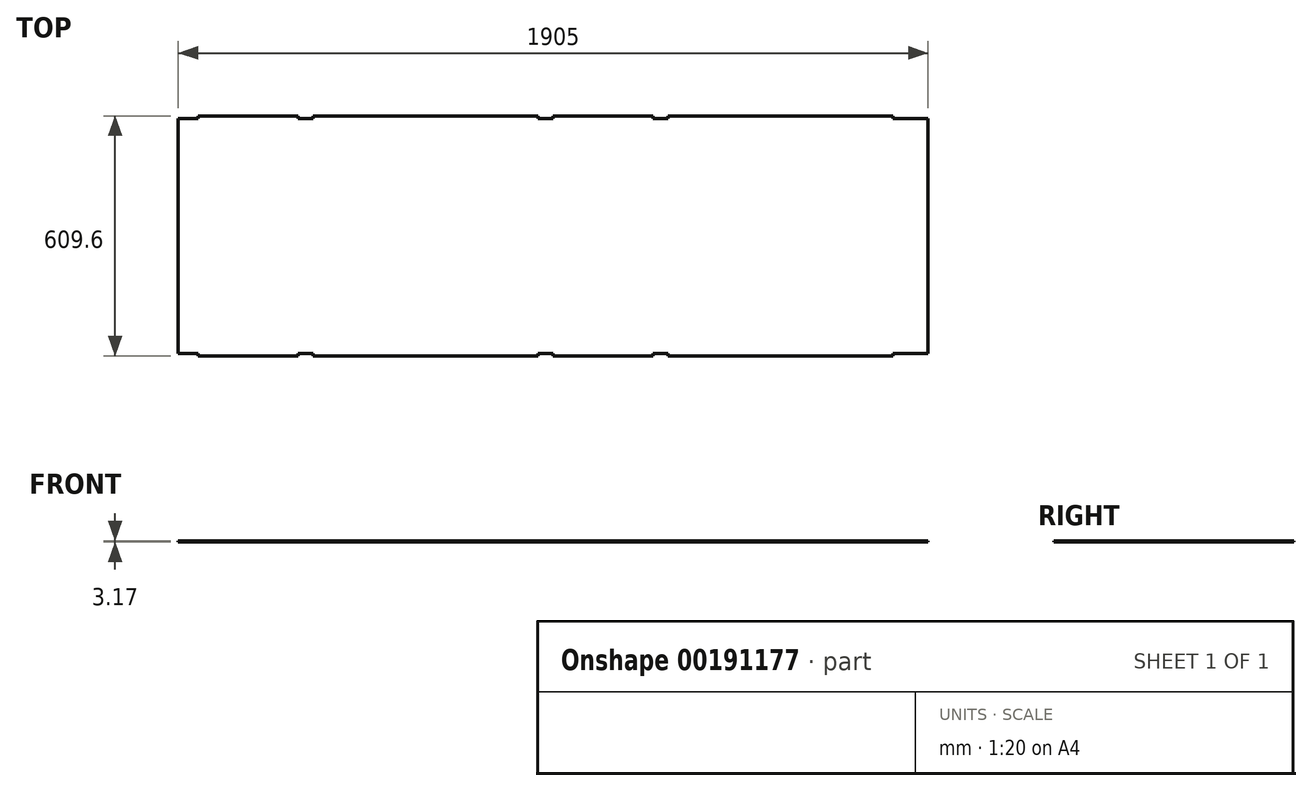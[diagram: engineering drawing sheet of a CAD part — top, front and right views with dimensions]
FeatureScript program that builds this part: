
annotation { "Feature Type Name" : "Feature", "Feature Type Description" : "" }
export const myFeature = defineFeature(function(context is Context, id is Id, definition is map)
    precondition{}
    {
        {
            var Q0;
            Q0=qCreatedBy(makeId("Top.planeOp"),FACE);
            var sketch = newSketch(context, id + "F0", { "sketchPlane" : qUnion([Q0])});
            skLineSegment(sketch, "E0.bottom", {"start": v(1276.35, -298.45) * mm, "end": v(-577.85, -298.45) * mm});
            skLineSegment(sketch, "E0.top", {"start": v(1276.35, 298.45) * mm, "end": v(-577.85, 298.45) * mm});
            skLineSegment(sketch, "E0.left", {"start": v(1276.35, -298.45) * mm, "end": v(1276.35, 298.45) * mm});
            skLineSegment(sketch, "E0.right", {"start": v(-577.85, -298.45) * mm, "end": v(-577.85, 298.45) * mm});
            skPoint(sketch, "E0.middle", {"position": v(349.25, 0) * mm});
            skLineSegment(sketch, "E1", {"start": v(615.95, 298.45) * mm, "end": v(615.95, -298.45) * mm, "construction": true});
            skLineSegment(sketch, "E2", {"start": v(577.85, 298.45) * mm, "end": v(577.85, -298.45) * mm, "construction": true});
            skLineSegment(sketch, "E3", {"start": v(-323.85, 298.45) * mm, "end": v(-323.85, -298.45) * mm, "construction": true});
            skLineSegment(sketch, "E4", {"start": v(-285.75, 298.45) * mm, "end": v(-285.75, -298.45) * mm, "construction": true});
            skLineSegment(sketch, "E5", {"start": v(285.75, 298.45) * mm, "end": v(285.75, -298.45) * mm, "construction": true});
            skLineSegment(sketch, "E6", {"start": v(323.85, 298.45) * mm, "end": v(323.85, -298.45) * mm, "construction": true});
            skLineSegment(sketch, "E7", {"start": v(1187.45, 298.45) * mm, "end": v(1187.45, -298.45) * mm, "construction": true});
            skSolve(sketch);
        }
        {
            var Q0;
            Q0 = qSketchRegion(id + "F0", true);
            extrude(context, id + "F1", {"entities" : qUnion([Q0]), "depth" : 3.17 * mm});
        }
        {
            var Q0;
            Q0=makeQuery(id+"F1.opExtrude","CAP_FACE",FACE,{"disambiguationData":[OSD([sQuery(id+"F0.wireOp",EDGE,"E0.bottom"),sQuery(id+"F0.wireOp",EDGE,"E0.top"),sQuery(id+"F0.wireOp",EDGE,"E0.left"),sQuery(id+"F0.wireOp",EDGE,"E0.right")])],"isStart":false});
            var sketch = newSketch(context, id + "F2", { "sketchPlane" : qUnion([Q0])});
            skLineSegment(sketch, "E8.bottom", {"start": v(1187.45, 298.45) * mm, "end": v(615.95, 298.45) * mm});
            skLineSegment(sketch, "E8.top", {"start": v(1187.45, 304.8) * mm, "end": v(615.95, 304.8) * mm});
            skLineSegment(sketch, "E8.left", {"start": v(1187.45, 298.45) * mm, "end": v(1187.45, 304.8) * mm});
            skLineSegment(sketch, "E8.right", {"start": v(615.95, 298.45) * mm, "end": v(615.95, 304.8) * mm});
            skLineSegment(sketch, "E9.bottom", {"start": v(577.85, 298.45) * mm, "end": v(323.85, 298.45) * mm});
            skLineSegment(sketch, "E9.top", {"start": v(577.85, 304.8) * mm, "end": v(323.85, 304.8) * mm});
            skLineSegment(sketch, "E9.left", {"start": v(577.85, 298.45) * mm, "end": v(577.85, 304.8) * mm});
            skLineSegment(sketch, "E9.right", {"start": v(323.85, 298.45) * mm, "end": v(323.85, 304.8) * mm});
            skLineSegment(sketch, "E10.bottom", {"start": v(285.75, 298.45) * mm, "end": v(-285.75, 298.45) * mm});
            skLineSegment(sketch, "E10.top", {"start": v(285.75, 304.8) * mm, "end": v(-285.75, 304.8) * mm});
            skLineSegment(sketch, "E10.left", {"start": v(285.75, 298.45) * mm, "end": v(285.75, 304.8) * mm});
            skLineSegment(sketch, "E10.right", {"start": v(-285.75, 298.45) * mm, "end": v(-285.75, 304.8) * mm});
            skLineSegment(sketch, "E11.bottom", {"start": v(-323.85, 298.45) * mm, "end": v(-577.85, 298.45) * mm});
            skLineSegment(sketch, "E11.top", {"start": v(-323.85, 304.8) * mm, "end": v(-577.85, 304.8) * mm});
            skLineSegment(sketch, "E11.left", {"start": v(-323.85, 298.45) * mm, "end": v(-323.85, 304.8) * mm});
            skLineSegment(sketch, "E11.right", {"start": v(-577.85, 298.45) * mm, "end": v(-577.85, 304.8) * mm});
            skLineSegment(sketch, "E12", {"start": v(-641.64, 0) * mm, "end": v(1319.37, 0) * mm, "construction": true});
            skLineSegment(sketch, "E13.MirrorCS", {"start": v(-577.85, -298.45) * mm, "end": v(-577.85, -304.8) * mm});
            skLineSegment(sketch, "E14.MirrorCS", {"start": v(-323.85, -304.8) * mm, "end": v(-577.85, -304.8) * mm});
            skLineSegment(sketch, "E15.MirrorCS", {"start": v(-323.85, -298.45) * mm, "end": v(-323.85, -304.8) * mm});
            skLineSegment(sketch, "E16.MirrorCS", {"start": v(-323.85, -298.45) * mm, "end": v(-577.85, -298.45) * mm});
            skLineSegment(sketch, "E17.MirrorCS", {"start": v(285.75, -298.45) * mm, "end": v(-285.75, -298.45) * mm});
            skLineSegment(sketch, "E18.MirrorCS", {"start": v(-285.75, -298.45) * mm, "end": v(-285.75, -304.8) * mm});
            skLineSegment(sketch, "E19.MirrorCS", {"start": v(285.75, -304.8) * mm, "end": v(-285.75, -304.8) * mm});
            skLineSegment(sketch, "E20.MirrorCS", {"start": v(285.75, -298.45) * mm, "end": v(285.75, -304.8) * mm});
            skLineSegment(sketch, "E21.MirrorCS", {"start": v(323.85, -298.45) * mm, "end": v(323.85, -304.8) * mm});
            skLineSegment(sketch, "E22.MirrorCS", {"start": v(577.85, -298.45) * mm, "end": v(323.85, -298.45) * mm});
            skLineSegment(sketch, "E23.MirrorCS", {"start": v(577.85, -304.8) * mm, "end": v(323.85, -304.8) * mm});
            skLineSegment(sketch, "E24.MirrorCS", {"start": v(577.85, -298.45) * mm, "end": v(577.85, -304.8) * mm});
            skLineSegment(sketch, "E25.MirrorCS", {"start": v(615.95, -298.45) * mm, "end": v(615.95, -304.8) * mm});
            skLineSegment(sketch, "E26.MirrorCS", {"start": v(1187.45, -298.45) * mm, "end": v(615.95, -298.45) * mm});
            skLineSegment(sketch, "E27.MirrorCS", {"start": v(1187.45, -304.8) * mm, "end": v(615.95, -304.8) * mm});
            skLineSegment(sketch, "E28.MirrorCS", {"start": v(1187.45, -298.45) * mm, "end": v(1187.45, -304.8) * mm});
            skLineSegment(sketch, "E29.bottom", {"start": v(-577.85, 298.45) * mm, "end": v(-628.65, 298.45) * mm});
            skLineSegment(sketch, "E29.top", {"start": v(-577.85, -298.45) * mm, "end": v(-628.65, -298.45) * mm});
            skLineSegment(sketch, "E29.left", {"start": v(-577.85, 298.45) * mm, "end": v(-577.85, -298.45) * mm});
            skLineSegment(sketch, "E29.right", {"start": v(-628.65, 298.45) * mm, "end": v(-628.65, -298.45) * mm});
            skSolve(sketch);
        }
        {
            var Q0;
            Q0 = qSketchRegion(id + "F2", true);
            extrude(context, id + "F3", {"entities" : qUnion([Q0]), "operationType" : NewBodyOperationType.ADD, "oppositeDirection" : true, "depth" : 3.17 * mm});
        }
    });
